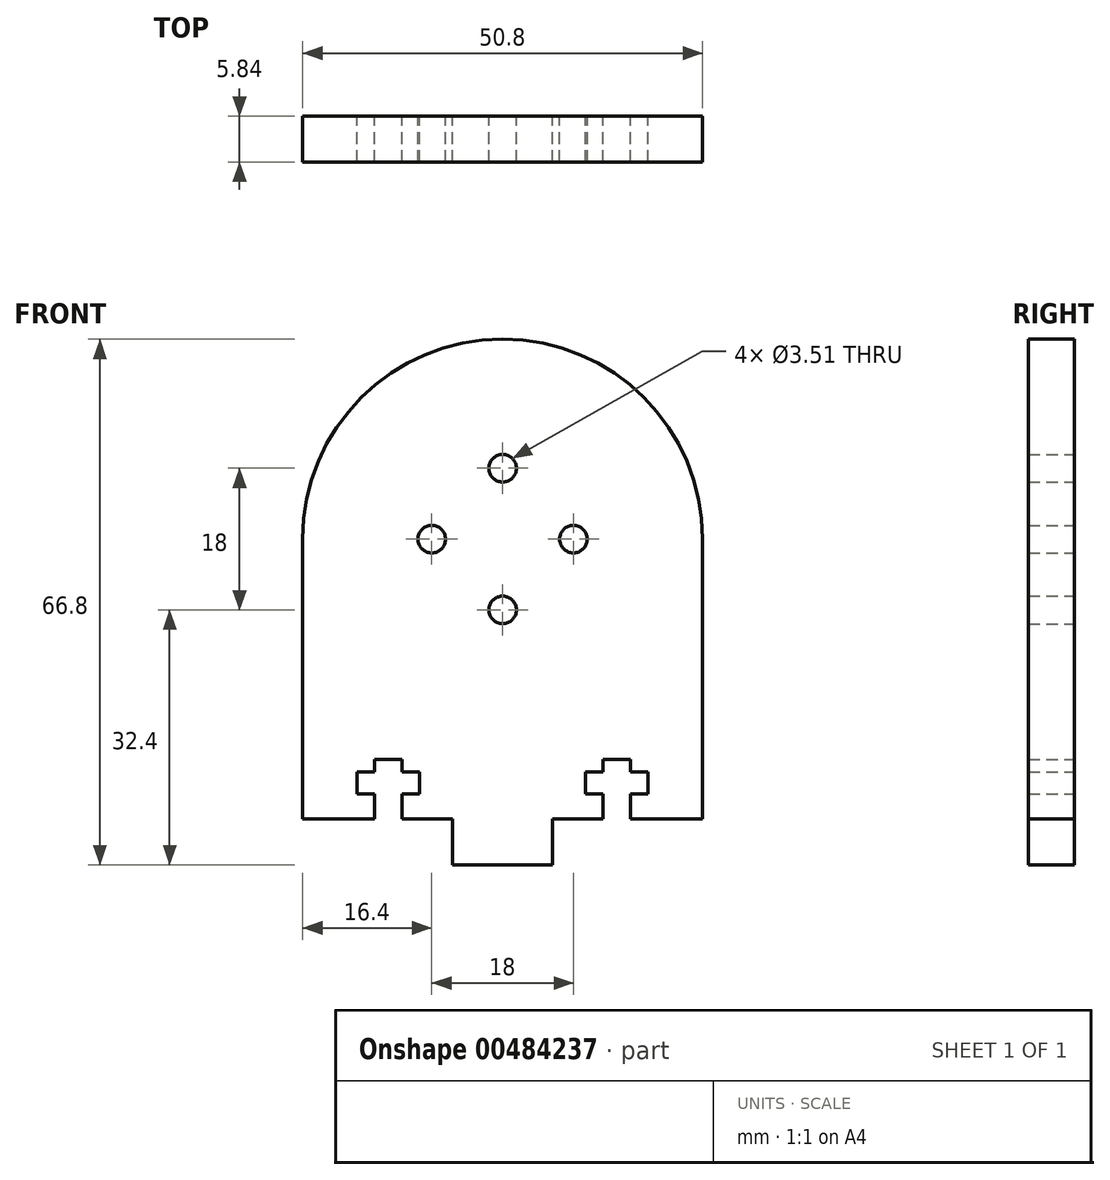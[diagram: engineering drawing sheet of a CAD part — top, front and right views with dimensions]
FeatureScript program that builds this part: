
annotation { "Feature Type Name" : "Feature", "Feature Type Description" : "" }
export const myFeature = defineFeature(function(context is Context, id is Id, definition is map)
    precondition{}
    {
        {
            var Q0;
            Q0=qCreatedBy(makeId("Front.planeOp"),FACE);
            var sketch = newSketch(context, id + "F0", { "sketchPlane" : qUnion([Q0])});
            skArc(sketch, "E0", {"start": v(-25.4, 0) * mm, "mid": v(0, 25.4) * mm, "end": v(25.4, 0) * mm});
            skCircle(sketch, "E1", {"center": v(0, 9) * mm, "radius": 1.75 * mm});
            skCircle(sketch, "E2.1.0", {"center": v(-9, 0) * mm, "radius": 1.75 * mm});
            skCircle(sketch, "E2.2.0", {"center": v(0, -9) * mm, "radius": 1.75 * mm});
            skCircle(sketch, "E2.3.0", {"center": v(9, 0) * mm, "radius": 1.75 * mm});
            skLineSegment(sketch, "E3.bottom", {"start": v(-25.4, 0) * mm, "end": v(25.4, 0) * mm, "construction": true});
            skLineSegment(sketch, "E3.top", {"start": v(-25.4, -35.56) * mm, "end": v(-16.25, -35.56) * mm});
            skLineSegment(sketch, "E3.left", {"start": v(-25.4, 0) * mm, "end": v(-25.4, -35.56) * mm});
            skLineSegment(sketch, "E3.right", {"start": v(25.4, 0) * mm, "end": v(25.4, -35.56) * mm});
            skLineSegment(sketch, "E4.top", {"start": v(-6.35, -41.4) * mm, "end": v(6.35, -41.4) * mm});
            skLineSegment(sketch, "E4.left", {"start": v(-6.35, -35.56) * mm, "end": v(-6.35, -41.4) * mm});
            skLineSegment(sketch, "E4.right", {"start": v(6.35, -35.56) * mm, "end": v(6.35, -41.4) * mm});
            skPoint(sketch, "E4.middle", {"position": v(0, -38.48) * mm});
            skLineSegment(sketch, "E5.trimOffspring", {"start": v(6.35, -35.56) * mm, "end": v(12.75, -35.56) * mm});
            skLineSegment(sketch, "E6", {"start": v(-14.5, -35.56) * mm, "end": v(-14.5, 0) * mm, "construction": true});
            skLineSegment(sketch, "E7.left", {"start": v(-16.25, -35.56) * mm, "end": v(-16.25, -32.39) * mm});
            skLineSegment(sketch, "E7.right", {"start": v(-12.75, -35.56) * mm, "end": v(-12.75, -32.39) * mm});
            skPoint(sketch, "E7.middle", {"position": v(-14.5, -33.97) * mm});
            skLineSegment(sketch, "E8.bottom", {"start": v(-18.47, -32.39) * mm, "end": v(-16.25, -32.39) * mm});
            skLineSegment(sketch, "E8.top", {"start": v(-18.47, -29.6) * mm, "end": v(-16.25, -29.6) * mm});
            skLineSegment(sketch, "E8.left", {"start": v(-18.47, -32.39) * mm, "end": v(-18.47, -29.6) * mm});
            skLineSegment(sketch, "E8.right", {"start": v(-10.53, -32.39) * mm, "end": v(-10.53, -29.6) * mm});
            skPoint(sketch, "E8.middle", {"position": v(-14.5, -31) * mm});
            skLineSegment(sketch, "E9.bottom", {"start": v(-16.25, -28.02) * mm, "end": v(-12.75, -28.02) * mm});
            skLineSegment(sketch, "E9.left", {"start": v(-16.25, -28.02) * mm, "end": v(-16.25, -29.6) * mm});
            skLineSegment(sketch, "E9.right", {"start": v(-12.75, -28.02) * mm, "end": v(-12.75, -29.6) * mm});
            skPoint(sketch, "E9.middle", {"position": v(-14.5, -28.81) * mm});
            skLineSegment(sketch, "E10.trimOffspring", {"start": v(-12.75, -32.39) * mm, "end": v(-10.53, -32.39) * mm});
            skLineSegment(sketch, "E11.trimOffspring", {"start": v(-12.75, -29.6) * mm, "end": v(-10.53, -29.6) * mm});
            skLineSegment(sketch, "E12.trimOffspring", {"start": v(-12.75, -35.56) * mm, "end": v(-6.35, -35.56) * mm});
            skPoint(sketch, "E13.MirrorP", {"position": v(14.5, -33.97) * mm});
            skLineSegment(sketch, "E14.MirrorCS", {"start": v(12.75, -28.02) * mm, "end": v(12.75, -29.6) * mm});
            skLineSegment(sketch, "E15.MirrorCS", {"start": v(12.75, -32.39) * mm, "end": v(10.53, -32.39) * mm});
            skPoint(sketch, "E16.MirrorP", {"position": v(14.5, -31) * mm});
            skPoint(sketch, "E17.MirrorP", {"position": v(14.5, -28.81) * mm});
            skLineSegment(sketch, "E18.MirrorCS", {"start": v(18.47, -29.6) * mm, "end": v(16.25, -29.6) * mm});
            skLineSegment(sketch, "E19.MirrorCS", {"start": v(16.25, -28.02) * mm, "end": v(12.75, -28.02) * mm});
            skLineSegment(sketch, "E20.MirrorCS", {"start": v(18.47, -32.39) * mm, "end": v(18.47, -29.6) * mm});
            skLineSegment(sketch, "E21.MirrorCS", {"start": v(18.47, -32.39) * mm, "end": v(16.25, -32.39) * mm});
            skLineSegment(sketch, "E22.MirrorCS", {"start": v(10.53, -32.39) * mm, "end": v(10.53, -29.6) * mm});
            skLineSegment(sketch, "E23.MirrorCS", {"start": v(16.25, -28.02) * mm, "end": v(16.25, -29.6) * mm});
            skLineSegment(sketch, "E24.MirrorCS", {"start": v(12.75, -29.6) * mm, "end": v(10.53, -29.6) * mm});
            skLineSegment(sketch, "E25.MirrorCS", {"start": v(12.75, -35.56) * mm, "end": v(12.75, -32.39) * mm});
            skLineSegment(sketch, "E26.MirrorCS", {"start": v(16.25, -35.56) * mm, "end": v(16.25, -32.39) * mm});
            skLineSegment(sketch, "E27.trimOffspring", {"start": v(16.25, -35.56) * mm, "end": v(25.4, -35.56) * mm});
            skSolve(sketch);
        }
        {
            var Q0;
            Q0 = qSketchRegion(id + "F0", true);
            extrude(context, id + "F1", {"entities" : qUnion([Q0]), "depth" : 5.84 * mm});
        }
    });
